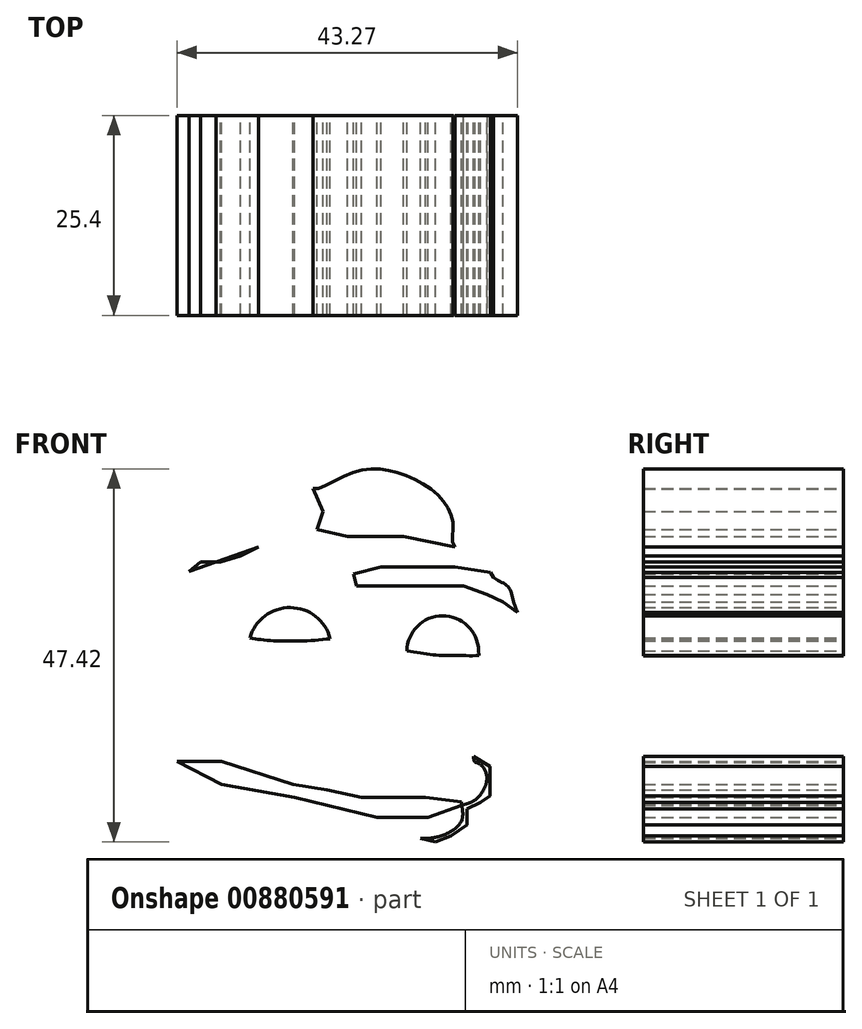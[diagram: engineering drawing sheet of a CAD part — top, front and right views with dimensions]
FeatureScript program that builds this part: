
annotation { "Feature Type Name" : "Feature", "Feature Type Description" : "" }
export const myFeature = defineFeature(function(context is Context, id is Id, definition is map)
    precondition{}
    {
        {
            var Q0;
            Q0=qCreatedBy(makeId("Front.planeOp"),FACE);
            var sketch = newSketch(context, id + "F0", { "sketchPlane" : qUnion([Q0])});
            skFitSpline(sketch, "E0", {"points": [v(-19.5, 21.87) * mm, v(-23.1, 19.5) * mm, v(-27.36, 14.48) * mm, v(-30.1, 9.84) * mm, v(-32.2, 3.7) * mm, v(-31.81, -8.14) * mm, v(-28.88, -12.3) * mm, v(-19.6, -17.13) * mm, v(-8.15, -20.07) * mm, v(1.98, -21.2) * mm, v(8.6, -20.64) * mm, v(9.36, -19.5) * mm, v(15.52, -18.65) * mm, v(20.35, -15.43) * mm, v(23.56, -15.53) * mm, v(26.97, -13.16) * mm, v(26.88, -10.98) * mm, v(27.73, -11.17) * mm, v(30.1, -8.24) * mm, v(28.58, -5.96) * mm, v(28.4, -3.98) * mm, v(26.03, 1.51) * mm, v(24.98, 3.03) * mm, v(26.69, 3.31) * mm, v(29.9, 5.68) * mm, v(32.46, 6.63) * mm, v(32.27, 8.14) * mm, v(34.07, 9.18) * mm, v(34.36, 12.02) * mm, v(33.6, 14.1) * mm, v(32.75, 16.38) * mm, v(30.95, 17.51) * mm, v(29.62, 19.6) * mm, v(26.03, 21.4) * mm, v(25.84, 24.04) * mm, v(24.04, 27.83) * mm, v(18.64, 30.86) * mm, v(12.96, 30.76) * mm, v(8.04, 28.78) * mm, v(6.9, 30.58) * mm, v(1.22, 33.8) * mm, v(-4.93, 34.08) * mm, v(-9.76, 32.28) * mm, v(-14.68, 28.97) * mm, v(-19.5, 21.87) * mm]});
            skFitSpline(sketch, "E1", {"points": [v(28.58, -5.96) * mm, v(25.55, -7.38) * mm, v(21.95, -7.76) * mm, v(15.9, -7.76) * mm, v(9.55, -7.1) * mm, v(1.5, -4.73) * mm, v(-6.73, -2.37) * mm, v(-11.18, -2.46) * mm, v(-13.16, -4.35) * mm, v(-14.4, -5.96) * mm, v(-14.2, -7.86) * mm, v(-11.46, -9.09) * mm, v(-9.28, -8.8) * mm, v(-7.01, -9.47) * mm, v(-3.6, -10.41) * mm, v(1.22, -11.93) * mm, v(5.67, -12.97) * mm, v(10.6, -13.82) * mm, v(15.42, -14.48) * mm, v(20.35, -15.43) * mm, v(23.56, -15.53) * mm, v(26.97, -13.16) * mm, v(26.88, -10.98) * mm, v(27.73, -11.17) * mm, v(30.1, -8.24) * mm, v(28.58, -5.96) * mm]});
            skFitSpline(sketch, "E2", {"points": [v(-6.84, 14.2) * mm, v(-5.23, 12.21) * mm, v(-1.54, 10.22) * mm, v(1.78, 9.56) * mm, v(7.27, 9.47) * mm, v(12.39, 10.13) * mm, v(13.43, 10.32) * mm, v(15.13, 9.09) * mm, v(19.3, 8.24) * mm, v(23.37, 7.67) * mm, v(26.69, 7.57) * mm, v(30, 7.67) * mm, v(31.24, 8.14) * mm, v(33.04, 9.18) * mm, v(34.07, 10.32) * mm, v(33.13, 12.02) * mm, v(26.88, 13.54) * mm, v(20.53, 14) * mm, v(14.37, 13.16) * mm, v(14.37, 14.39) * mm, v(12.39, 15.15) * mm, v(7.93, 15.24) * mm, v(3.48, 14.96) * mm, v(-3.15, 14.39) * mm, v(-6.84, 14.2) * mm]});
            skArc(sketch, "E3", {"start": v(10.2, 9.72) * mm, "mid": v(5.13, 13.67) * mm, "end": v(0, 9.8) * mm});
            skArc(sketch, "E4", {"start": v(29.06, 8.24) * mm, "mid": v(24.46, 12.63) * mm, "end": v(19.94, 8.15) * mm});
            skArc(sketch, "E5", {"start": v(-7.22, 10.32) * mm, "mid": v(2.8, 6.33) * mm, "end": v(13.43, 8.24) * mm});
            skLineSegment(sketch, "E6", {"start": v(-9.02, 24.7) * mm, "end": v(-4.29, 26.6) * mm});
            skLineSegment(sketch, "E7", {"start": v(-4.29, 26.6) * mm, "end": v(-0.97, 26.6) * mm});
            skLineSegment(sketch, "E8", {"start": v(-0.97, 26.6) * mm, "end": v(3.1, 26.6) * mm});
            skLineSegment(sketch, "E9", {"start": v(3.1, 26.6) * mm, "end": v(4.78, 25.89) * mm});
            skLineSegment(sketch, "E10", {"start": v(4.78, 25.89) * mm, "end": v(8.5, 23.57) * mm});
            skLineSegment(sketch, "E11", {"start": v(8.5, 23.57) * mm, "end": v(11.25, 20.26) * mm});
            skLineSegment(sketch, "E12", {"start": v(11.25, 20.26) * mm, "end": v(8.5, 23.57) * mm});
            skLineSegment(sketch, "E13", {"start": v(8.5, 23.57) * mm, "end": v(12.39, 22.72) * mm});
            skLineSegment(sketch, "E14", {"start": v(12.39, 22.72) * mm, "end": v(15.51, 22.72) * mm});
            skLineSegment(sketch, "E15", {"start": v(15.51, 22.72) * mm, "end": v(19.49, 22.72) * mm});
            skLineSegment(sketch, "E16", {"start": v(19.49, 22.72) * mm, "end": v(26.03, 21.4) * mm});
            skLineSegment(sketch, "E17", {"start": v(11.25, 20.26) * mm, "end": v(8.5, 21.4) * mm});
            skLineSegment(sketch, "E18", {"start": v(8.5, 21.4) * mm, "end": v(6.32, 21.4) * mm});
            skLineSegment(sketch, "E19", {"start": v(6.32, 21.4) * mm, "end": v(3.95, 21.4) * mm});
            skLineSegment(sketch, "E20", {"start": v(3.95, 21.4) * mm, "end": v(1.11, 21.4) * mm});
            skLineSegment(sketch, "E21", {"start": v(1.11, 21.4) * mm, "end": v(-1.16, 20.26) * mm});
            skLineSegment(sketch, "E22", {"start": v(-1.16, 20.26) * mm, "end": v(-3.72, 19.5) * mm});
            skLineSegment(sketch, "E23", {"start": v(-3.72, 19.5) * mm, "end": v(-6.28, 19.5) * mm});
            skLineSegment(sketch, "E24", {"start": v(-6.28, 19.5) * mm, "end": v(-7.75, 18.28) * mm});
            skLineSegment(sketch, "E25", {"start": v(-7.75, 18.28) * mm, "end": v(1.11, 21.4) * mm});
            skLineSegment(sketch, "E26", {"start": v(11.25, 20.26) * mm, "end": v(13.14, 17.97) * mm});
            skLineSegment(sketch, "E27", {"start": v(13.14, 17.97) * mm, "end": v(16.65, 18.84) * mm});
            skLineSegment(sketch, "E28", {"start": v(16.65, 18.84) * mm, "end": v(20.15, 18.84) * mm});
            skLineSegment(sketch, "E29", {"start": v(20.15, 18.84) * mm, "end": v(22.8, 18.84) * mm});
            skLineSegment(sketch, "E30", {"start": v(22.8, 18.84) * mm, "end": v(26.03, 18.84) * mm});
            skLineSegment(sketch, "E31", {"start": v(26.03, 18.84) * mm, "end": v(30.56, 18.12) * mm});
            skLineSegment(sketch, "E32", {"start": v(30.56, 18.12) * mm, "end": v(30.95, 17.51) * mm});
            skLineSegment(sketch, "E33", {"start": v(13.14, 17.97) * mm, "end": v(13.92, 14.84) * mm});
            skLineSegment(sketch, "E34", {"start": v(13.92, 14.84) * mm, "end": v(12.58, 17.51) * mm});
            skLineSegment(sketch, "E35", {"start": v(12.58, 17.51) * mm, "end": v(11.25, 17.51) * mm});
            skLineSegment(sketch, "E36", {"start": v(11.25, 17.51) * mm, "end": v(8.04, 18.84) * mm});
            skLineSegment(sketch, "E37", {"start": v(8.04, 18.84) * mm, "end": v(4.78, 18.84) * mm});
            skLineSegment(sketch, "E38", {"start": v(4.78, 18.84) * mm, "end": v(1.4, 18.74) * mm});
            skLineSegment(sketch, "E39", {"start": v(1.4, 18.74) * mm, "end": v(-1.72, 17.97) * mm});
            skLineSegment(sketch, "E40", {"start": v(-1.72, 17.97) * mm, "end": v(-4.2, 15.92) * mm});
            skLineSegment(sketch, "E41", {"start": v(-4.2, 15.92) * mm, "end": v(-7.5, 15.92) * mm});
            skLineSegment(sketch, "E42", {"start": v(-7.5, 15.92) * mm, "end": v(-11.3, 15.92) * mm});
            skLineSegment(sketch, "E43", {"start": v(-11.3, 15.92) * mm, "end": v(-10.9, 15.11) * mm});
            skLineSegment(sketch, "E44", {"start": v(-10.9, 15.11) * mm, "end": v(-8.37, 14.07) * mm});
            skLineSegment(sketch, "E45", {"start": v(-8.37, 14.07) * mm, "end": v(-6.84, 13.91) * mm});
            skLineSegment(sketch, "E46", {"start": v(13.53, 16.4) * mm, "end": v(24.7, 16.4) * mm});
            skLineSegment(sketch, "E47", {"start": v(24.7, 16.4) * mm, "end": v(27.16, 16.4) * mm});
            skLineSegment(sketch, "E48", {"start": v(27.16, 16.4) * mm, "end": v(30.1, 15.35) * mm});
            skLineSegment(sketch, "E49", {"start": v(30.1, 15.35) * mm, "end": v(32.18, 14.39) * mm});
            skLineSegment(sketch, "E50", {"start": v(32.18, 14.39) * mm, "end": v(34, 13.06) * mm});
            skLineSegment(sketch, "E51", {"start": v(0, 3.12) * mm, "end": v(7.36, 4.73) * mm});
            skLineSegment(sketch, "E52", {"start": v(7.36, 4.73) * mm, "end": v(8.03, 4.55) * mm});
            skLineSegment(sketch, "E53", {"start": v(14.47, 4.45) * mm, "end": v(19.11, 1.05) * mm});
            skLineSegment(sketch, "E54", {"start": v(19.11, 1.05) * mm, "end": v(16.79, 2.75) * mm});
            skLineSegment(sketch, "E55", {"start": v(16.79, 2.75) * mm, "end": v(24.98, 3.03) * mm});
            skLineSegment(sketch, "E56", {"start": v(-17.17, -7.4) * mm, "end": v(-17.17, -10.23) * mm});
            skLineSegment(sketch, "E57", {"start": v(-17.17, -10.23) * mm, "end": v(-14.53, -12.17) * mm});
            skLineSegment(sketch, "E58", {"start": v(-14.53, -12.17) * mm, "end": v(-12.34, -12.17) * mm});
            skLineSegment(sketch, "E59", {"start": v(8.04, 28.78) * mm, "end": v(9.26, 25.89) * mm});
            skLineSegment(sketch, "E60", {"start": v(9.26, 25.89) * mm, "end": v(8.5, 23.57) * mm});
            skLineSegment(sketch, "E61", {"start": v(-20.1, 16.27) * mm, "end": v(-20.1, 18.45) * mm});
            skLineSegment(sketch, "E62", {"start": v(-20.1, 18.45) * mm, "end": v(-19.5, 21.87) * mm});
            skLineSegment(sketch, "E63", {"start": v(-9.28, -5.88) * mm, "end": v(-3.6, -5.88) * mm});
            skLineSegment(sketch, "E64", {"start": v(-3.6, -5.88) * mm, "end": v(5.47, -8.8) * mm});
            skLineSegment(sketch, "E65", {"start": v(5.47, -8.8) * mm, "end": v(9.83, -9.47) * mm});
            skLineSegment(sketch, "E66", {"start": v(9.83, -9.47) * mm, "end": v(14.18, -10.41) * mm});
            skLineSegment(sketch, "E67", {"start": v(14.18, -10.41) * mm, "end": v(18.16, -10.41) * mm});
            skLineSegment(sketch, "E68", {"start": v(18.16, -10.41) * mm, "end": v(22.33, -10.41) * mm});
            skLineSegment(sketch, "E69", {"start": v(22.33, -10.41) * mm, "end": v(26.88, -10.98) * mm});
            skLineSegment(sketch, "E70", {"start": v(29.06, 8.24) * mm, "end": v(29.08, 7.58) * mm});
            skLineSegment(sketch, "E71", {"start": v(-9.28, -5.88) * mm, "end": v(-3.6, -8.8) * mm});
            skLineSegment(sketch, "E72", {"start": v(-3.6, -8.8) * mm, "end": v(5.67, -10.41) * mm});
            skLineSegment(sketch, "E73", {"start": v(5.67, -10.41) * mm, "end": v(16.17, -12.97) * mm});
            skPoint(sketch, "E73.endSnap0", {"position": v(16.17, -10.41) * mm});
            skLineSegment(sketch, "E74", {"start": v(16.17, -12.97) * mm, "end": v(22.62, -12.97) * mm});
            skLineSegment(sketch, "E75", {"start": v(22.62, -12.97) * mm, "end": v(27.73, -11.17) * mm});
            skLineSegment(sketch, "E76", {"start": v(28.4, -5.22) * mm, "end": v(30.51, -6.5) * mm});
            skLineSegment(sketch, "E77", {"start": v(30.51, -6.5) * mm, "end": v(30.51, -8) * mm});
            skLineSegment(sketch, "E78", {"start": v(30.51, -8) * mm, "end": v(30.51, -10.26) * mm});
            skLineSegment(sketch, "E79", {"start": v(30.51, -10.26) * mm, "end": v(29.3, -11.1) * mm});
            skLineSegment(sketch, "E80", {"start": v(29.3, -11.1) * mm, "end": v(27.58, -11.92) * mm});
            skLineSegment(sketch, "E81", {"start": v(27.58, -11.92) * mm, "end": v(27.58, -13.95) * mm});
            skLineSegment(sketch, "E82", {"start": v(27.58, -13.95) * mm, "end": v(25.55, -15.3) * mm});
            skLineSegment(sketch, "E83", {"start": v(25.55, -15.3) * mm, "end": v(23.6, -16.12) * mm});
            skLineSegment(sketch, "E84", {"start": v(23.6, -16.12) * mm, "end": v(21.64, -15.64) * mm});
            skLineSegment(sketch, "E85", {"start": v(21.64, -15.64) * mm, "end": v(20.35, -15.43) * mm});
            skSolve(sketch);
        }
        {
            var Q0;
            {var subQ0=sQuery(id+"F0.wireOp",EDGE,"E3");Q0=makeQuery(id+"F0.imprint","IMPRINT",FACE,{"disambiguationData":[TD([[makeQuery(id+"F0.imprint","IMPRINT",EDGE,{"derivedFrom":subQ0}),1.0]])]});}
            var Q1;
            {var subQ0=sQuery(id+"F0.wireOp",EDGE,"E4");Q1=makeQuery(id+"F0.imprint","IMPRINT",FACE,{"disambiguationData":[TD([[makeQuery(id+"F0.imprint","IMPRINT",EDGE,{"derivedFrom":subQ0}),1.0]])]});}
            var Q2;
            Q2=makeQuery(id+"F0.imprint","IMPRINT",FACE,{"disambiguationData":[TD([[makeQuery(id+"F0.imprint","IMPRINT",EDGE,{"derivedFrom":sQuery(id+"F0.wireOp",EDGE,"E12")}),-1.0]])]});
            var Q3;
            {var subQ2=sQuery(id+"F0.wireOp",EDGE,"E27");Q3=makeQuery(id+"F0.imprint","IMPRINT",FACE,{"disambiguationData":[TD([[makeQuery(id+"F0.imprint","IMPRINT",EDGE,{"derivedFrom":subQ2}),-1.0]])]});}
            var Q4;
            Q4=makeQuery(id+"F0.imprint","IMPRINT",FACE,{"disambiguationData":[TD([[makeQuery(id+"F0.imprint","IMPRINT",EDGE,{"derivedFrom":sQuery(id+"F0.wireOp",EDGE,"E13")}),1.0]])]});
            var Q5;
            Q5=makeQuery(id+"F0.imprint","IMPRINT",FACE,{"disambiguationData":[TD([[makeQuery(id+"F0.imprint","IMPRINT",EDGE,{"derivedFrom":sQuery(id+"F0.wireOp",EDGE,"E12")}),1.0]])]});
            var Q6;
            {var subQ0=sQuery(id+"F0.wireOp",EDGE,"E1");var subQ1=sQuery(id+"F0.wireOp",EDGE,"E0");var subQ2=makeQuery(id+"F0.imprint","INTERSECT",VERTEX,{"disambiguationData":[OD(3.0)],"derivedFrom":[subQ1,subQ0]});Q6=makeQuery(id+"F0.imprint","IMPRINT",FACE,{"disambiguationData":[TD([[makeQuery(id+"F0.imprint","IMPRINT",EDGE,{"disambiguationData":[TD([[subQ2,-1.0]])],"derivedFrom":subQ1}),1.0]])]});}
            var Q7;
            {var subQ0=sQuery(id+"F0.wireOp",EDGE,"E1");var subQ1=sQuery(id+"F0.wireOp",EDGE,"E0");var subQ2=makeQuery(id+"F0.imprint","INTERSECT",VERTEX,{"disambiguationData":[OD(2.0)],"derivedFrom":[subQ1,subQ0]});Q7=makeQuery(id+"F0.imprint","IMPRINT",FACE,{"disambiguationData":[TD([[makeQuery(id+"F0.imprint","IMPRINT",EDGE,{"disambiguationData":[TD([[subQ2,-1.0]])],"derivedFrom":subQ1}),-1.0]])]});}
            var Q8;
            {var subQ0=sQuery(id+"F0.wireOp",EDGE,"E1");var subQ1=sQuery(id+"F0.wireOp",EDGE,"E0");var subQ2=makeQuery(id+"F0.imprint","INTERSECT",VERTEX,{"disambiguationData":[OD(4.0)],"derivedFrom":[subQ1,subQ0]});Q8=makeQuery(id+"F0.imprint","IMPRINT",FACE,{"disambiguationData":[TD([[makeQuery(id+"F0.imprint","IMPRINT",EDGE,{"disambiguationData":[TD([[subQ2,-1.0]])],"derivedFrom":subQ1}),-1.0]])]});}
            var Q9;
            {var subQ0=sQuery(id+"F0.wireOp",EDGE,"E1");var subQ1=sQuery(id+"F0.wireOp",EDGE,"E0");var subQ2=makeQuery(id+"F0.imprint","INTERSECT",VERTEX,{"disambiguationData":[OD(6.0)],"derivedFrom":[subQ1,subQ0]});Q9=makeQuery(id+"F0.imprint","IMPRINT",FACE,{"disambiguationData":[TD([[makeQuery(id+"F0.imprint","IMPRINT",EDGE,{"disambiguationData":[TD([[subQ2,-1.0]])],"derivedFrom":subQ1}),-1.0]])]});}
            var Q10;
            {var subQ0=sQuery(id+"F0.wireOp",EDGE,"E1");var subQ1=sQuery(id+"F0.wireOp",EDGE,"E0");var subQ2=makeQuery(id+"F0.imprint","INTERSECT",VERTEX,{"disambiguationData":[OD(7.0)],"derivedFrom":[subQ1,subQ0]});Q10=makeQuery(id+"F0.imprint","IMPRINT",FACE,{"disambiguationData":[TD([[makeQuery(id+"F0.imprint","IMPRINT",EDGE,{"disambiguationData":[TD([[subQ2,-1.0]])],"derivedFrom":subQ1}),1.0]])]});}
            var Q11;
            {var subQ0=sQuery(id+"F0.wireOp",EDGE,"E1");var subQ1=sQuery(id+"F0.wireOp",EDGE,"E0");var subQ2=makeQuery(id+"F0.imprint","INTERSECT",VERTEX,{"disambiguationData":[OD(8.0)],"derivedFrom":[subQ1,subQ0]});Q11=makeQuery(id+"F0.imprint","IMPRINT",FACE,{"disambiguationData":[TD([[makeQuery(id+"F0.imprint","IMPRINT",EDGE,{"disambiguationData":[TD([[subQ2,-1.0]])],"derivedFrom":subQ1}),-1.0]])]});}
            var Q12;
            {var subQ0=sQuery(id+"F0.wireOp",EDGE,"E21");Q12=makeQuery(id+"F0.imprint","IMPRINT",FACE,{"disambiguationData":[TD([[makeQuery(id+"F0.imprint","IMPRINT",EDGE,{"derivedFrom":subQ0}),-1.0]])]});}
            var Q13;
            {var subQ0=sQuery(id+"F0.wireOp",EDGE,"E24");Q13=makeQuery(id+"F0.imprint","IMPRINT",FACE,{"disambiguationData":[TD([[makeQuery(id+"F0.imprint","IMPRINT",EDGE,{"derivedFrom":subQ0}),1.0]])]});}
            var Q14;
            {var subQ0=sQuery(id+"F0.wireOp",EDGE,"E32");Q14=makeQuery(id+"F0.imprint","IMPRINT",FACE,{"disambiguationData":[TD([[makeQuery(id+"F0.imprint","IMPRINT",EDGE,{"derivedFrom":subQ0}),-1.0]])]});}
            var Q15;
            Q15=makeQuery(id+"F0.imprint","IMPRINT",FACE,{"disambiguationData":[TD([[makeQuery(id+"F0.imprint","IMPRINT",EDGE,{"derivedFrom":sQuery(id+"F0.wireOp",EDGE,"E63")}),-1.0]])]});
            extrude(context, id + "F1", {"entities" : qUnion([Q0, Q1, Q2, Q3, Q4, Q5, Q6, Q7, Q8, Q9, Q10, Q11, Q12, Q13, Q14, Q15]), "depth" : 25.4 * mm, "offsetDistance" : 25.4 * mm});
        }
    });
